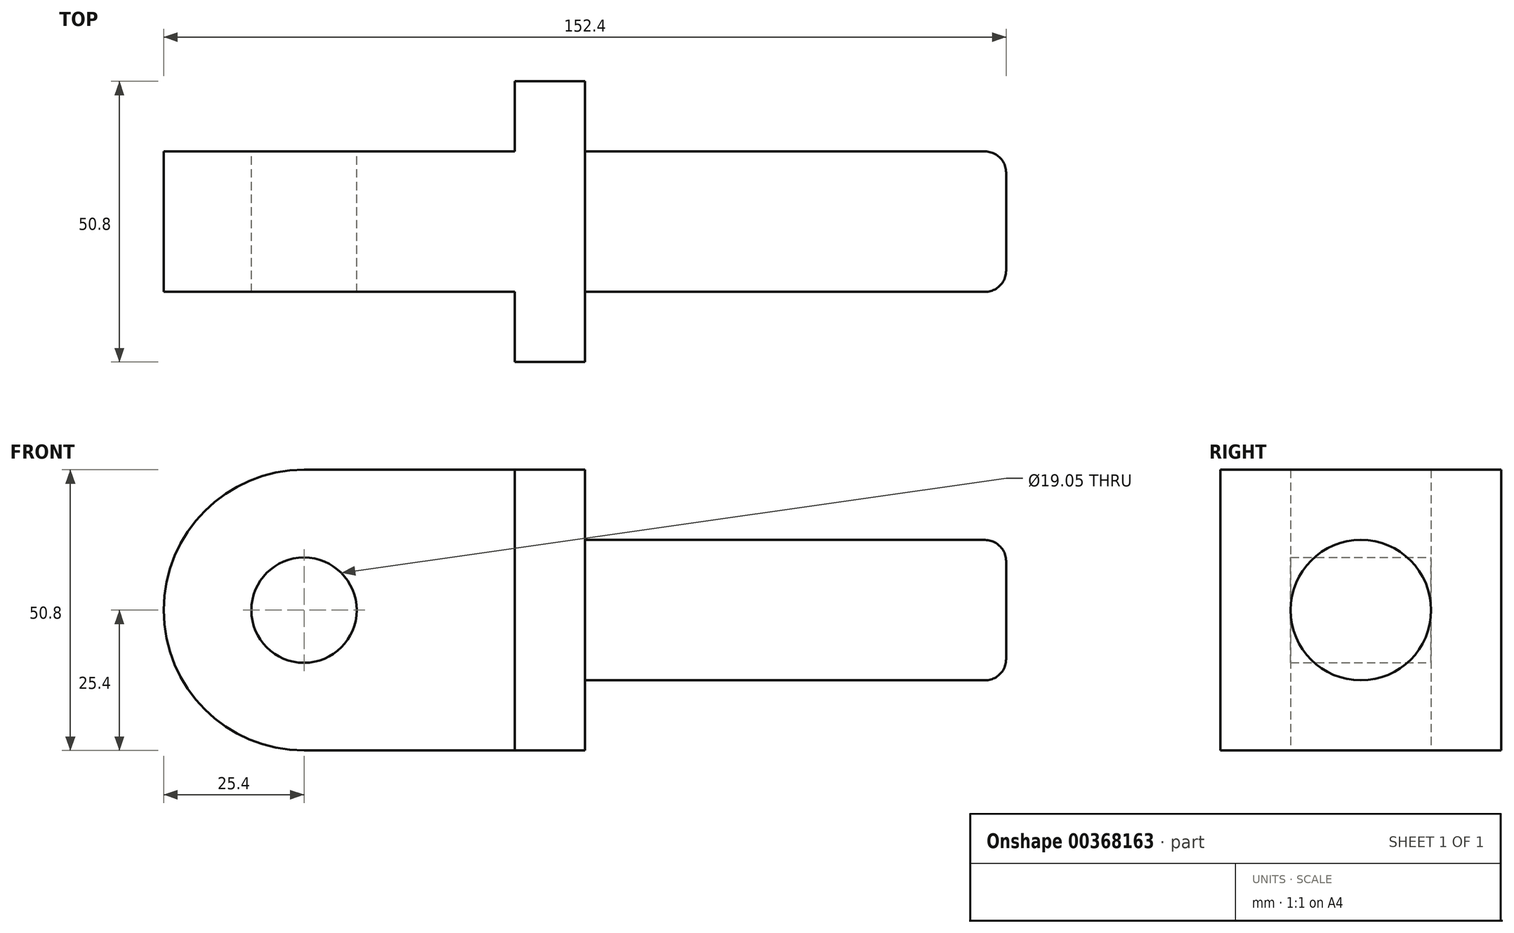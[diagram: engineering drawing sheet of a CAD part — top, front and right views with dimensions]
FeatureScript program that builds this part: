
annotation { "Feature Type Name" : "Feature", "Feature Type Description" : "" }
export const myFeature = defineFeature(function(context is Context, id is Id, definition is map)
    precondition{}
    {
        {
            var Q0;
            Q0=qCreatedBy(makeId("Front.planeOp"),FACE);
            var sketch = newSketch(context, id + "F0", { "sketchPlane" : qUnion([Q0])});
            skCircle(sketch, "E0", {"center": v(0, 0) * mm, "radius": 9.53 * mm});
            skLineSegment(sketch, "E1", {"start": v(0, 25.4) * mm, "end": v(38.1, 25.4) * mm});
            skLineSegment(sketch, "E2", {"start": v(38.1, 25.4) * mm, "end": v(38.1, -25.4) * mm});
            skLineSegment(sketch, "E3", {"start": v(38.1, -25.4) * mm, "end": v(0, -25.4) * mm});
            skArc(sketch, "E4", {"start": v(0, 25.4) * mm, "mid": v(-25.4, 0) * mm, "end": v(0, -25.4) * mm});
            skSolve(sketch);
        }
        {
            var Q0;
            Q0 = qSketchRegion(id + "F0", true);
            extrude(context, id + "F1", {"entities" : qUnion([Q0]), "depth" : 25.4 * mm});
        }
        {
            var Q0;
            Q0=makeQuery(id+"F1.opExtrude","SWEPT_FACE",FACE,{"disambiguationData":[OSD([sQuery(id+"F0.wireOp",EDGE,"E2")])]});
            var sketch = newSketch(context, id + "F2", { "sketchPlane" : qUnion([Q0])});
            skLineSegment(sketch, "E5", {"start": v(0, 25.4) * mm, "end": v(12.7, 25.4) * mm});
            skLineSegment(sketch, "E6", {"start": v(12.7, 25.4) * mm, "end": v(12.7, -25.4) * mm});
            skLineSegment(sketch, "E7", {"start": v(12.7, -25.4) * mm, "end": v(0, -25.4) * mm});
            skLineSegment(sketch, "E8", {"start": v(0, -25.4) * mm, "end": v(-25.4, -25.4) * mm});
            skLineSegment(sketch, "E9", {"start": v(-25.4, -25.4) * mm, "end": v(-38.1, -25.4) * mm});
            skLineSegment(sketch, "E10", {"start": v(-38.1, -25.4) * mm, "end": v(-38.1, 25.4) * mm});
            skLineSegment(sketch, "E11", {"start": v(-38.1, 25.4) * mm, "end": v(-25.4, 25.4) * mm});
            skLineSegment(sketch, "E12", {"start": v(-25.4, 25.4) * mm, "end": v(0, 25.4) * mm});
            skSolve(sketch);
        }
        {
            var Q0;
            Q0 = qSketchRegion(id + "F2", true);
            extrude(context, id + "F3", {"entities" : qUnion([Q0]), "operationType" : NewBodyOperationType.ADD, "depth" : 12.7 * mm});
        }
        {
            var Q0;
            Q0=makeQuery(id+"F3.opExtrude","CAP_FACE",FACE,{"disambiguationData":[OSD([sQuery(id+"F2.wireOp",EDGE,"E5"),sQuery(id+"F2.wireOp",EDGE,"E6"),sQuery(id+"F2.wireOp",EDGE,"E7"),sQuery(id+"F2.wireOp",EDGE,"E8"),sQuery(id+"F2.wireOp",EDGE,"E9"),sQuery(id+"F2.wireOp",EDGE,"E10"),sQuery(id+"F2.wireOp",EDGE,"E11"),sQuery(id+"F2.wireOp",EDGE,"E12")])],"isStart":false});
            var sketch = newSketch(context, id + "F4", { "sketchPlane" : qUnion([Q0])});
            skCircle(sketch, "E13", {"center": v(-12.7, 0) * mm, "radius": 12.7 * mm});
            skSolve(sketch);
        }
        {
            var Q0;
            Q0=makeQuery(id+"F4.imprint","IMPRINT",FACE,{"disambiguationData":[TD([[makeQuery(id+"F4.imprint","IMPRINT",EDGE,{"derivedFrom":sQuery(id+"F4.wireOp",EDGE,"E13")}),1.0]])]});
            extrude(context, id + "F5", {"entities" : qUnion([Q0]), "operationType" : NewBodyOperationType.ADD, "depth" : 76.2 * mm});
        }
        {
            var Q0;
            Q0=makeQuery(id+"F5.opExtrude","CAP_EDGE",EDGE,{"disambiguationData":[OSD([sQuery(id+"F4.wireOp",EDGE,"E13")])],"isStart":false});
            var Q1;
            Q1=makeQuery(id+"F5.opExtrude","CAP_EDGE",EDGE,{"disambiguationData":[OSD([sQuery(id+"F4.wireOp",EDGE,"E13")])],"isStart":true});
            fillet(context, id + "F6", {"entities" : qUnion([Q0, Q1]), "radius" : 3.8 * mm, "tangentPropagation" : true, "allowEdgeOverflow" : false});
        }
    });
